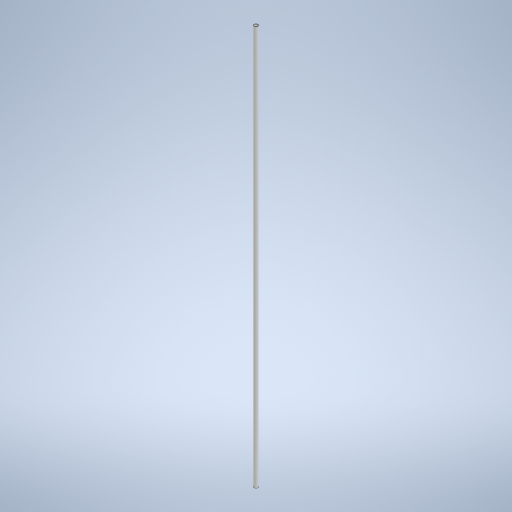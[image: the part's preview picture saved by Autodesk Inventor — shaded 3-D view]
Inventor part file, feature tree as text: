
AUTODESK INVENTOR PART (.ipt)
format: ipt  version: 2023 (Build 270158000, 158)  size: 235,008 bytes
history: native  units: in
note: dims shown in document units (in); Inventor stores cm internally (conversion verified against a paired STEP export)
features: extrude x1, sketch x1
ambient origin geometry x8: Origin, YZ Plane, XZ Plane, XY Plane, X Axis, Y Axis, Z Axis, Center Point
bodies: Solide1 (feature_tree)
feature tree (2):
  extrude  "Extrusion1"  Depth=0.3937in
  sketch  "Esquisse1"
